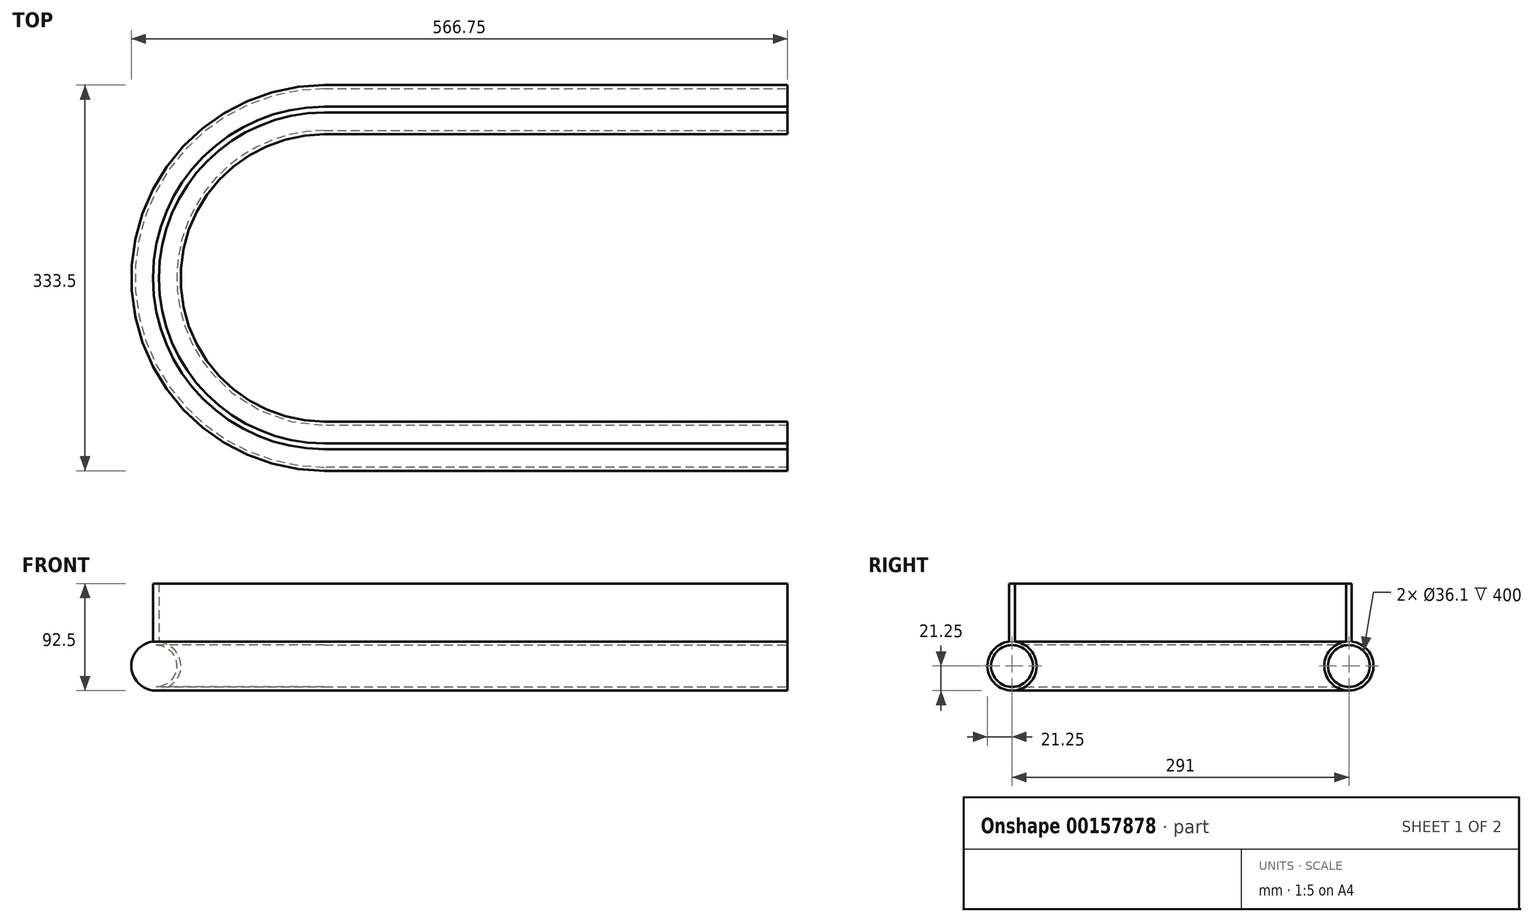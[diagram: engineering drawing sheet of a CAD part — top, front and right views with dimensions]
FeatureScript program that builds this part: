
annotation { "Feature Type Name" : "Feature", "Feature Type Description" : "" }
export const myFeature = defineFeature(function(context is Context, id is Id, definition is map)
    precondition{}
    {
        {
            var Q0;
            Q0=qCreatedBy(makeId("Top.planeOp"),FACE);
            var sketch = newSketch(context, id + "F0", { "sketchPlane" : qUnion([Q0])});
            skLineSegment(sketch, "E0", {"start": v(-400, 145.5) * mm, "end": v(0, 145.5) * mm});
            skArc(sketch, "E1", {"start": v(-400, 145.5) * mm, "mid": v(-545.5, 0) * mm, "end": v(-400, -145.5) * mm});
            skLineSegment(sketch, "E2", {"start": v(-400, -145.5) * mm, "end": v(0, -145.5) * mm});
            skSolve(sketch);
        }
        {
            var Q0;
            Q0=qCreatedBy(makeId("Right.planeOp"),FACE);
            var sketch = newSketch(context, id + "F1", { "sketchPlane" : qUnion([Q0])});
            skArc(sketch, "E3", {"start": v(-148, -0.15) * mm, "mid": v(-145.5, -42.5) * mm, "end": v(-143, -0.15) * mm});
            skLineSegment(sketch, "E4.0", {"start": v(-145.5, 0) * mm, "end": v(0, 0) * mm, "construction": true});
            skLineSegment(sketch, "E5.bottom", {"start": v(-148, 50) * mm, "end": v(-143, 50) * mm});
            skLineSegment(sketch, "E5.left", {"start": v(-148, 50) * mm, "end": v(-148, -0.15) * mm});
            skLineSegment(sketch, "E5.right", {"start": v(-143, 50) * mm, "end": v(-143, -0.15) * mm});
            skLineSegment(sketch, "E6", {"start": v(-145.5, 50) * mm, "end": v(-145.5, -1.76) * mm, "construction": true});
            skLineSegment(sketch, "E7", {"start": v(-145.5, -21.25) * mm, "end": v(-145.5, 90.65) * mm, "construction": true});
            skCircle(sketch, "E8", {"center": v(-145.5, -21.25) * mm, "radius": 18.05 * mm});
            skSolve(sketch);
        }
        {
            var Q0;
            Q0=makeQuery(id+"F1.imprint","IMPRINT",FACE,{"disambiguationData":[TD([[makeQuery(id+"F1.imprint","IMPRINT",EDGE,{"derivedFrom":sQuery(id+"F1.wireOp",EDGE,"E3")}),1.0]])]});
            var Q1;
            Q1=sQuery(id+"F0.wireOp",EDGE,"E2");
            var Q2;
            Q2=sQuery(id+"F0.wireOp",EDGE,"E1");
            var Q3;
            Q3=sQuery(id+"F0.wireOp",EDGE,"E0");
            sweep(context, id + "F2", {"profiles" : qUnion([Q0]), "path" : qUnion([Q1, Q2, Q3])});
        }
    });
